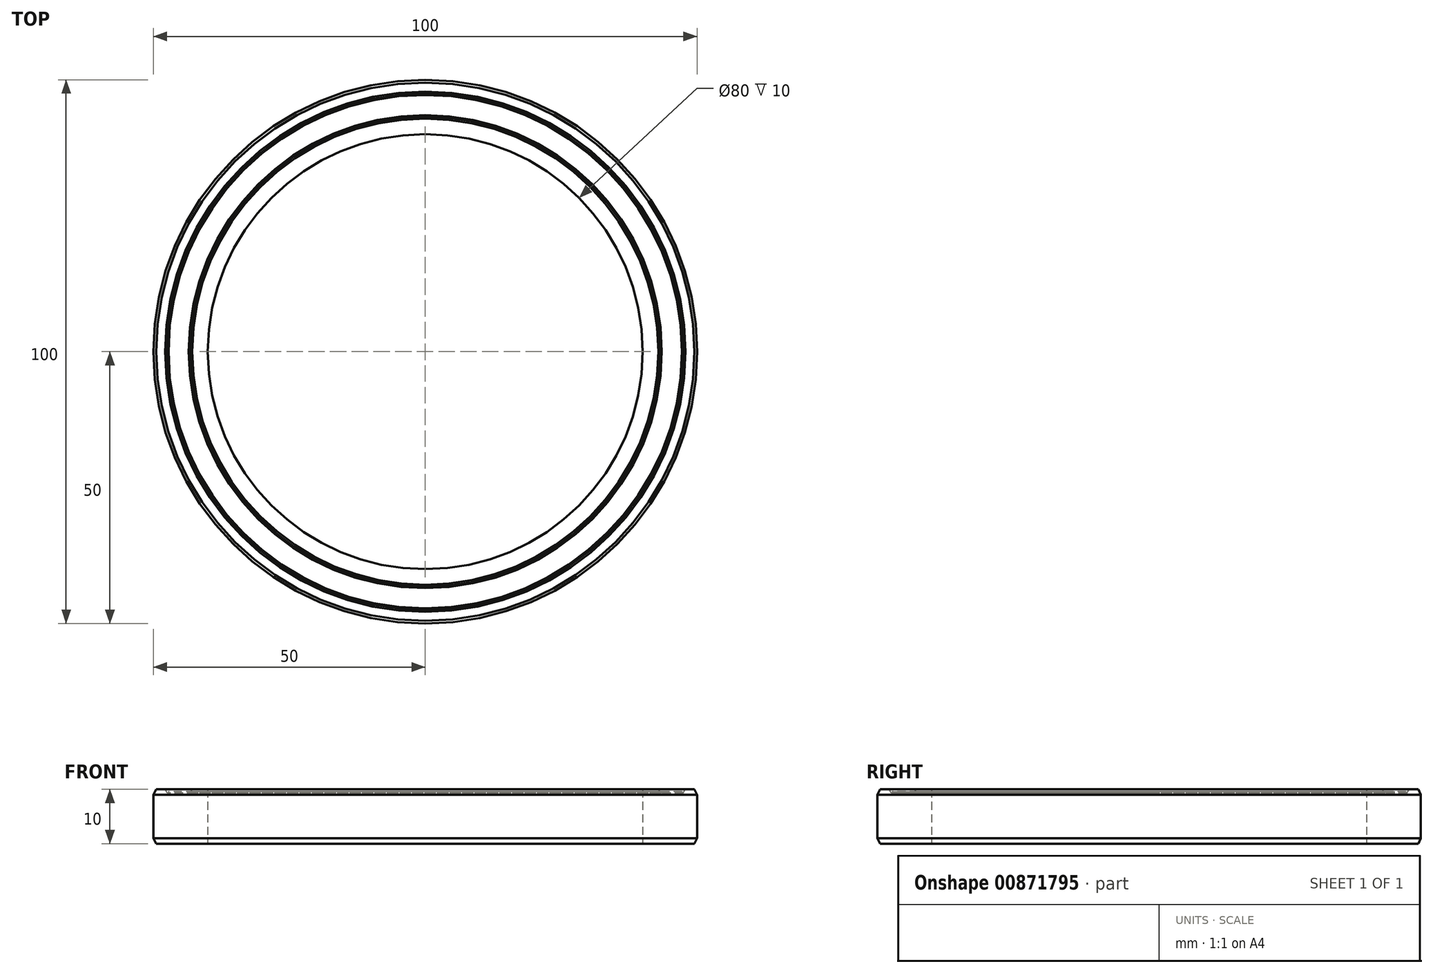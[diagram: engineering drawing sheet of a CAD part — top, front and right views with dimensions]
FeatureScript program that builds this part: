
annotation { "Feature Type Name" : "Feature", "Feature Type Description" : "" }
export const myFeature = defineFeature(function(context is Context, id is Id, definition is map)
    precondition{}
    {
        {
            var Q0;
            Q0=qCreatedBy(makeId("Top.planeOp"),FACE);
            var sketch = newSketch(context, id + "F0", { "sketchPlane" : qUnion([Q0])});
            skCircle(sketch, "E0", {"center": v(0, 0) * mm, "radius": 40 * mm});
            skCircle(sketch, "E1", {"center": v(0, 0) * mm, "radius": 50 * mm});
            skSolve(sketch);
        }
        {
            var Q0;
            Q0=makeQuery(id+"F0.imprint","IMPRINT",FACE,{"disambiguationData":[TD([[makeQuery(id+"F0.imprint","IMPRINT",EDGE,{"derivedFrom":sQuery(id+"F0.wireOp",EDGE,"E0")}),-1.0]])]});
            extrude(context, id + "F1", {"entities" : qUnion([Q0]), "depth" : 10 * mm, "offsetDistance" : 25 * mm});
        }
        {
            var Q0;
            Q0=qCreatedBy(makeId("Front.planeOp"),FACE);
            var sketch = newSketch(context, id + "F2", { "sketchPlane" : qUnion([Q0])});
            skLineSegment(sketch, "E2", {"start": v(-50, 10) * mm, "end": v(-47.85, 10) * mm});
            skLineSegment(sketch, "E3", {"start": v(-47.46, 9.33) * mm, "end": v(-47.85, 10) * mm});
            skLineSegment(sketch, "E4", {"start": v(-47.46, 9.33) * mm, "end": v(-47.36, 9.33) * mm});
            skLineSegment(sketch, "E5", {"start": v(-47.23, 9.56) * mm, "end": v(-47.36, 9.33) * mm});
            skLineSegment(sketch, "E6", {"start": v(-47.23, 9.56) * mm, "end": v(-43.5, 9.56) * mm});
            skLineSegment(sketch, "E7", {"start": v(-43.5, 9.56) * mm, "end": v(-43.37, 9.33) * mm});
            skLineSegment(sketch, "E8", {"start": v(-43.37, 9.33) * mm, "end": v(-43.27, 9.33) * mm});
            skLineSegment(sketch, "E9", {"start": v(-43.27, 9.33) * mm, "end": v(-42.88, 10) * mm});
            skLineSegment(sketch, "E10", {"start": v(-42.88, 10) * mm, "end": v(-40, 10) * mm});
            skLineSegment(sketch, "E11", {"start": v(-40, 10) * mm, "end": v(-40, 13.41) * mm});
            skLineSegment(sketch, "E12", {"start": v(-40, 13.41) * mm, "end": v(-50, 13.41) * mm});
            skLineSegment(sketch, "E13", {"start": v(-50, 13.41) * mm, "end": v(-50, 10) * mm});
            skLineSegment(sketch, "E14", {"start": v(-47.4, 10.36) * mm, "end": v(-47.4, 9.36) * mm, "construction": true});
            skPoint(sketch, "E14.endSnap0", {"position": v(-47.4, 9.33) * mm});
            skLineSegment(sketch, "E15", {"start": v(-43.32, 10.77) * mm, "end": v(-43.32, 8.2) * mm, "construction": true});
            skLineSegment(sketch, "E16", {"start": v(0, 7.44) * mm, "end": v(0, 14.41) * mm, "construction": true});
            skSolve(sketch);
        }
        {
            var Q0;
            Q0=makeQuery(id+"F2.imprint","IMPRINT",FACE,{"disambiguationData":[TD([[makeQuery(id+"F2.imprint","IMPRINT",EDGE,{"derivedFrom":sQuery(id+"F2.wireOp",EDGE,"E2")}),1.0]])]});
            var Q1;
            Q1=sQuery(id+"F2.wireOp",EDGE,"E16");
            revolve(context, id + "F3", {"operationType" : NewBodyOperationType.REMOVE, "surfaceOperationType" : NewSurfaceOperationType.NEW, "entities" : qUnion([Q0]), "axis" : qUnion([Q1]), "revolveType" : RevolveType.FULL, "oppositeDirection" : true});
        }
        {
            var Q0;
            {var subQ0=sQuery(id+"F0.wireOp",EDGE,"E1");Q0=makeQuery(id+"F3.boolean.opBoolean","SPLIT",FACE,{"disambiguationData":[TD([makeQuery(id+"F1.opExtrude","SWEPT_FACE",FACE,{"disambiguationData":[OSD([subQ0])]})])],"derivedFrom":makeQuery(id+"F1.opExtrude","CAP_FACE",FACE,{"disambiguationData":[OSD([sQuery(id+"F0.wireOp",EDGE,"E0"),subQ0])],"isStart":false})});}
            var Q1;
            Q1=makeQuery(id+"F1.opExtrude","CAP_FACE",FACE,{"disambiguationData":[OSD([sQuery(id+"F0.wireOp",EDGE,"E0"),sQuery(id+"F0.wireOp",EDGE,"E1")])],"isStart":true});
            cPlane(context, id + "F4", {"entities" : qUnion([Q0, Q1]), "cplaneType" : CPlaneType.MID_PLANE, "offset" : 25 * mm, "width" : 150 * mm, "height" : 150 * mm});
        }
        {
            var Q0;
            Q0=makeQuery(id+"F1.opExtrude","CAP_EDGE",EDGE,{"disambiguationData":[OSD([sQuery(id+"F0.wireOp",EDGE,"E1")])],"isStart":false});
            var Q1;
            Q1=makeQuery(id+"F1.opExtrude","CAP_EDGE",EDGE,{"disambiguationData":[OSD([sQuery(id+"F0.wireOp",EDGE,"E1")])],"isStart":true});
            chamfer(context, id + "F5", {"entities" : qUnion([Q0, Q1]), "chamferType" : ChamferType.TWO_OFFSETS, "width1" : 1 * mm, "oppositeDirection" : true, "width2" : .5 * mm, "tangentPropagation" : true});
        }
    });
